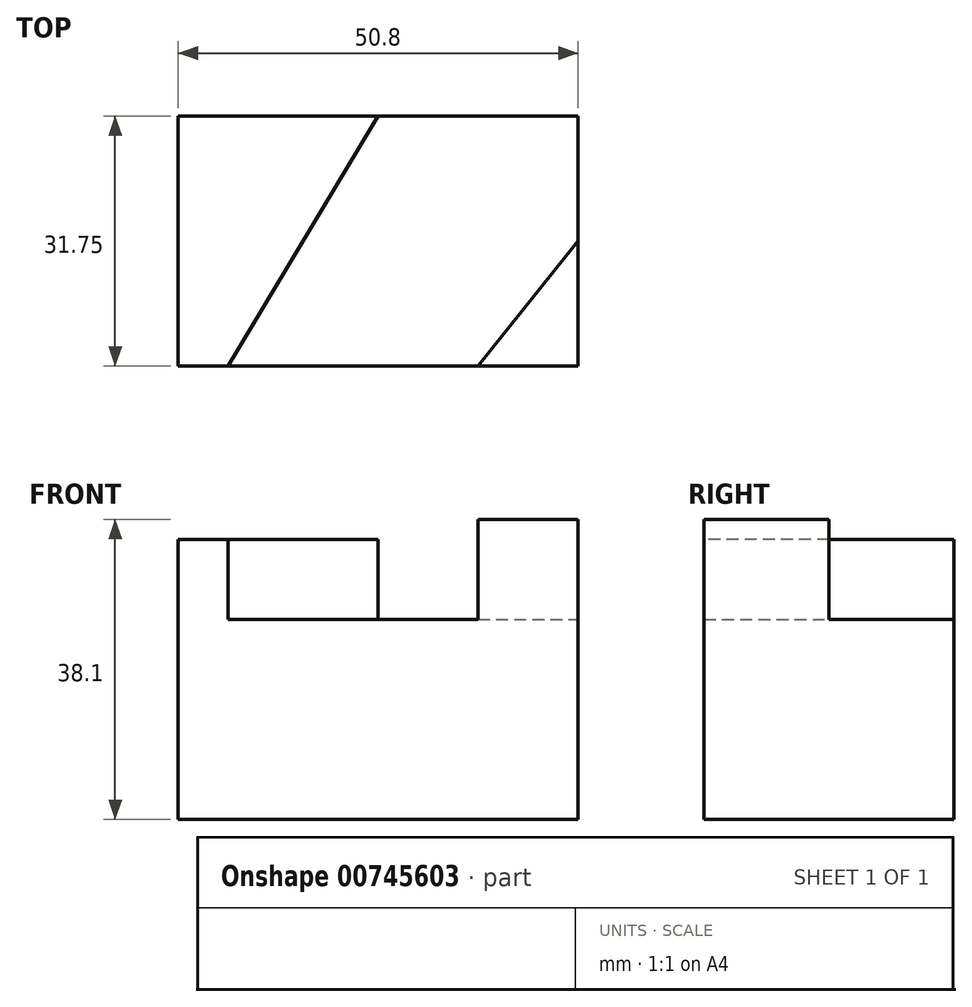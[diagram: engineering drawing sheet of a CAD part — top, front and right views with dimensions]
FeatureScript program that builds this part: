
annotation { "Feature Type Name" : "Feature", "Feature Type Description" : "" }
export const myFeature = defineFeature(function(context is Context, id is Id, definition is map)
    precondition{}
    {
        {
            var Q0;
            Q0=qCreatedBy(makeId("Top.planeOp"),FACE);
            var sketch = newSketch(context, id + "F0", { "sketchPlane" : qUnion([Q0])});
            skLineSegment(sketch, "E0", {"start": v(0, 0) * mm, "end": v(0, 31.75) * mm});
            skLineSegment(sketch, "E1", {"start": v(0, 31.75) * mm, "end": v(50.8, 31.75) * mm});
            skLineSegment(sketch, "E2", {"start": v(50.8, 31.75) * mm, "end": v(50.8, 0) * mm});
            skLineSegment(sketch, "E3", {"start": v(50.8, 0) * mm, "end": v(0, 0) * mm});
            skSolve(sketch);
        }
        {
            var Q0;
            Q0 = qSketchRegion(id + "F0", true);
            extrude(context, id + "F1", {"entities" : qUnion([Q0]), "depth" : 25.4 * mm, "offsetDistance" : 25.4 * mm});
        }
        {
            var Q0;
            Q0=makeQuery(id+"F1.opExtrude","CAP_FACE",FACE,{"disambiguationData":[OSD([sQuery(id+"F0.wireOp",EDGE,"E0"),sQuery(id+"F0.wireOp",EDGE,"E1"),sQuery(id+"F0.wireOp",EDGE,"E2"),sQuery(id+"F0.wireOp",EDGE,"E3")])],"isStart":false});
            var sketch = newSketch(context, id + "F2", { "sketchPlane" : qUnion([Q0])});
            skLineSegment(sketch, "E4", {"start": v(0, 31.75) * mm, "end": v(25.4, 31.75) * mm});
            skLineSegment(sketch, "E5", {"start": v(25.4, 31.75) * mm, "end": v(6.35, 0) * mm});
            skLineSegment(sketch, "E6", {"start": v(0, 0) * mm, "end": v(6.35, 0) * mm});
            skLineSegment(sketch, "E7", {"start": v(0, 31.75) * mm, "end": v(0, 0) * mm});
            skLineSegment(sketch, "E8", {"start": v(50.8, 19.05) * mm, "end": v(38.1, 0) * mm});
            skLineSegment(sketch, "E9", {"start": v(38.1, 0) * mm, "end": v(50.8, 0) * mm});
            skLineSegment(sketch, "E10", {"start": v(50.8, 0) * mm, "end": v(50.8, 19.05) * mm});
            skSolve(sketch);
        }
        {
            var Q0;
            Q0=makeQuery(id+"F2.imprint","IMPRINT",FACE,{"disambiguationData":[TD([[makeQuery(id+"F2.imprint","IMPRINT",EDGE,{"derivedFrom":sQuery(id+"F2.wireOp",EDGE,"E4")}),-1.0]])]});
            extrude(context, id + "F3", {"entities" : qUnion([Q0]), "operationType" : NewBodyOperationType.ADD, "depth" : 10.16 * mm, "offsetDistance" : 25.4 * mm});
        }
        {
            var Q0;
            Q0=makeQuery(id+"F1.opExtrude","CAP_FACE",FACE,{"disambiguationData":[OSD([sQuery(id+"F0.wireOp",EDGE,"E0"),sQuery(id+"F0.wireOp",EDGE,"E1"),sQuery(id+"F0.wireOp",EDGE,"E2"),sQuery(id+"F0.wireOp",EDGE,"E3")])],"isStart":false});
            var sketch = newSketch(context, id + "F4", { "sketchPlane" : qUnion([Q0])});
            skLineSegment(sketch, "E11", {"start": v(38.1, 0) * mm, "end": v(50.8, 15.88) * mm});
            skLineSegment(sketch, "E12", {"start": v(50.8, 15.88) * mm, "end": v(50.8, 0) * mm});
            skLineSegment(sketch, "E13", {"start": v(50.8, 0) * mm, "end": v(38.1, 0) * mm});
            skSolve(sketch);
        }
        {
            var Q0;
            Q0=makeQuery(id+"F4.imprint","IMPRINT",FACE,{"disambiguationData":[TD([[makeQuery(id+"F4.imprint","IMPRINT",EDGE,{"derivedFrom":sQuery(id+"F4.wireOp",EDGE,"E11")}),-1.0]])]});
            extrude(context, id + "F5", {"entities" : qUnion([Q0]), "operationType" : NewBodyOperationType.ADD, "depth" : 12.7 * mm, "offsetDistance" : 25.4 * mm});
        }
    });
